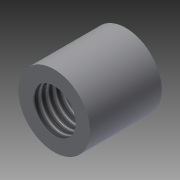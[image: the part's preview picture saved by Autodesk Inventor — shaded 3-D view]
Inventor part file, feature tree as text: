
AUTODESK INVENTOR PART (.ipt)
format: ipt  version: 2015 SP1 (Build 190203100, 203)  size: 83,456 bytes
history: native  units: mm
features: extrude x1, thread x1, sketch x1
ambient origin geometry x8: Origin, YZ Plane, XZ Plane, XY Plane, X Axis, Y Axis, Z Axis, Center Point
bodies: Solid1 (feature_tree)
feature tree (3):
  extrude  "Extrusion1"  Depth=10.0mm
  thread  "Thread1"  [1 undecoded]
  sketch  "Sketch1"  dims[d0=5.0mm d1=3.0mm d2=5.0mm d3=0.0mm d4=10.0mm d5=0.0mm]
note: 1 required parameter value undecoded (feature->parameter linkage not recoverable at this tier; creation-order binding heuristic only, values carry confidence <= 0.55)
